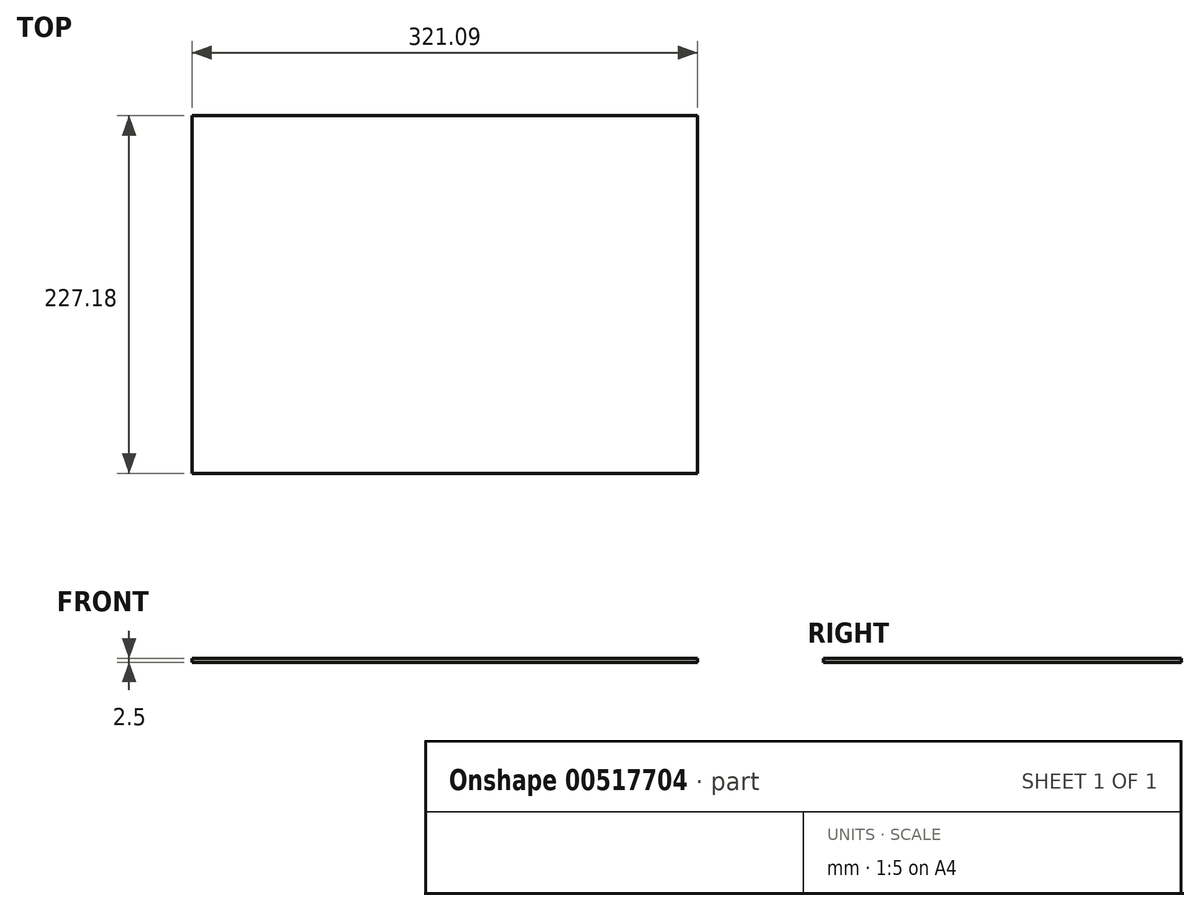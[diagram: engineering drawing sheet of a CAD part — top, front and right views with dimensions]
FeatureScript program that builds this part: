
annotation { "Feature Type Name" : "Feature", "Feature Type Description" : "" }
export const myFeature = defineFeature(function(context is Context, id is Id, definition is map)
    precondition{}
    {
        {
            var Q0;
            Q0=qCreatedBy(makeId("Top.planeOp"),FACE);
            var sketch = newSketch(context, id + "F0", { "sketchPlane" : qUnion([Q0])});
            skLineSegment(sketch, "E0.bottom", {"start": v(-131.1, 73.85) * mm, "end": v(190, 73.85) * mm});
            skLineSegment(sketch, "E0.top", {"start": v(-131.1, -153.33) * mm, "end": v(190, -153.33) * mm});
            skLineSegment(sketch, "E0.left", {"start": v(-131.1, 73.85) * mm, "end": v(-131.1, -153.33) * mm});
            skLineSegment(sketch, "E0.right", {"start": v(190, 73.85) * mm, "end": v(190, -153.33) * mm});
            skSolve(sketch);
        }
        {
            var Q0;
            Q0 = qSketchRegion(id + "F0", true);
            extrude(context, id + "F1", {"entities" : qUnion([Q0]), "oppositeDirection" : true, "depth" : 2.5 * mm, "offsetDistance" : 25 * mm});
        }
    });
